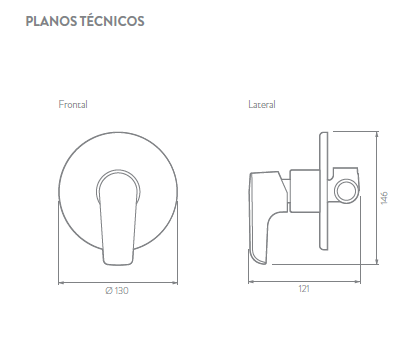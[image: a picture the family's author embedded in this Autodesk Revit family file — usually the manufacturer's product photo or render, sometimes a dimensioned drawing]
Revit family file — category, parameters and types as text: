
# Revit family: CA4055551_Mezclador Monocontrol Cascade SSB
name_source: partatom
category: Plumbing Fixtures
units: mm (PartAtom-declared; Revit-internal decimal feet)

## family parameters
Always vertical = Yes
Cut with Voids When Loaded = No
OmniClass Number = 23.31.11.17.15
OmniClass Title = Shower Disc Faucets
Part Type = Normal
Room Calculation Point = No
Round Connector Dimension = Use Diameter
Shared = No
Work Plane-Based = No

## types (1)
- CA4055551_Mezclador Monocontrol Cascade SSB
    Años de garantía acabados = a años
    Capacidad de flujo máximo = 80 psi.
    Creado por = IDD
    Description = La línea de griferías y accesorios plásticos Cascade se inspira en la fluidez natural
del agua y las formas creadas a su paso en caídas y cascadas, sus líneas fluidas
crean un solo viaje alrededor del producto generando formas limpias y un
acabado perfecto que resalta la precisión del diseño • Tecnología Duracrome: acabado superior, mayor espesor en el cromado que
lo hace más brillante y resistente a la corrosión.
• Fácil limpieza: diseño que evita la acumulación de impurezas.
    Fecha de creación = 21/07/2020
    Garantía = 30 años
    Manufacturer = Corona
    Material = Corona_Cromado
    Model = Mezclador monocontrol SD CASCADE
    Peso neto = 650 g. - 1,43 lb
    Presión máxima recomendada = 125 psi (862 Kpa).
    Presión mínima recomendada = 20 psi (138 Kpa).
    Temperatura de uso = 5˚C a 71˚C.
    URL = https://corona.co
    Vida útil o desgaste (unidad) = 250.000 ciclos

## geometry (parser evidence)
native form markers: Sweep x4
no freeform markers — native parametric forms only
